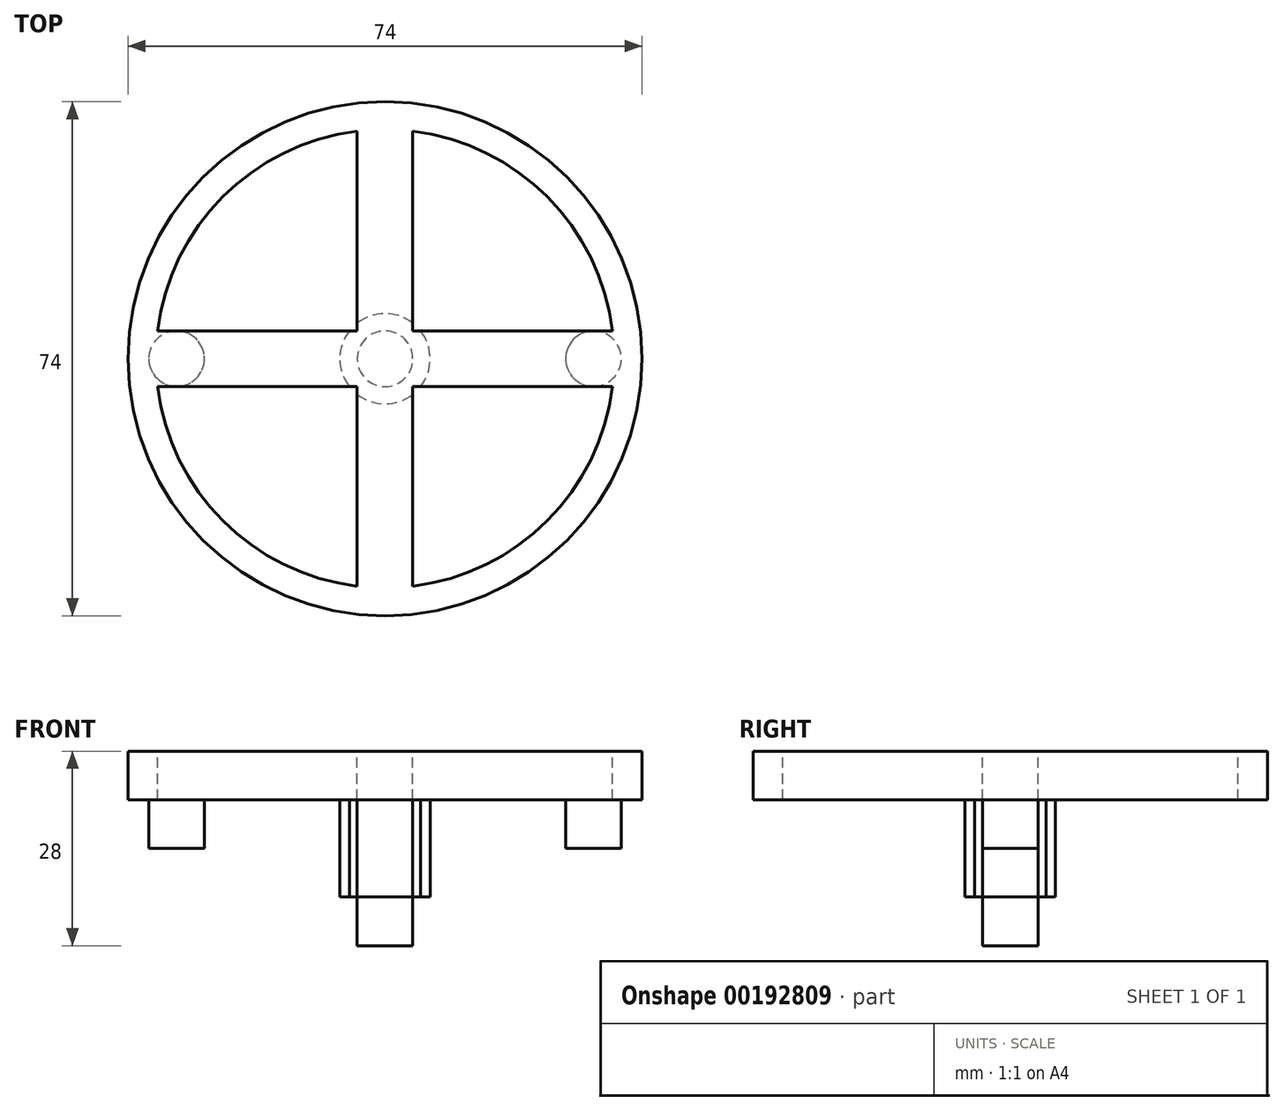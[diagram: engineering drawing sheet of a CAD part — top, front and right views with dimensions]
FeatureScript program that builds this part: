
annotation { "Feature Type Name" : "Feature", "Feature Type Description" : "" }
export const myFeature = defineFeature(function(context is Context, id is Id, definition is map)
    precondition{}
    {
        {
            var Q0;
            Q0=qCreatedBy(makeId("Top.planeOp"),FACE);
            var sketch = newSketch(context, id + "F0", { "sketchPlane" : qUnion([Q0])});
            skCircle(sketch, "E0", {"center": v(0, 0) * mm, "radius": 37 * mm});
            skSolve(sketch);
        }
        {
            var Q0;
            Q0 = qSketchRegion(id + "F0", true);
            extrude(context, id + "F1", {"entities" : qUnion([Q0]), "depth" : 7 * mm});
        }
        {
            var Q0;
            Q0=makeQuery(id+"F1.opExtrude","CAP_FACE",FACE,{"disambiguationData":[OSD([sQuery(id+"F0.wireOp",EDGE,"E0")])],"isStart":true});
            var sketch = newSketch(context, id + "F2", { "sketchPlane" : qUnion([Q0])});
            skCircle(sketch, "E1", {"center": v(0, 0) * mm, "radius": 4 * mm});
            skSolve(sketch);
        }
        {
            var Q0;
            Q0 = qSketchRegion(id + "F2", true);
            extrude(context, id + "F3", {"entities" : qUnion([Q0]), "operationType" : NewBodyOperationType.ADD, "depth" : 21 * mm});
        }
        {
            var Q0;
            Q0=makeQuery(id+"F1.opExtrude","CAP_FACE",FACE,{"disambiguationData":[OSD([sQuery(id+"F0.wireOp",EDGE,"E0")])],"isStart":true});
            var sketch = newSketch(context, id + "F4", { "sketchPlane" : qUnion([Q0])});
            skCircle(sketch, "E2", {"center": v(-30, 0) * mm, "radius": 4 * mm});
            skCircle(sketch, "E3", {"center": v(30, 0) * mm, "radius": 4 * mm});
            skSolve(sketch);
        }
        {
            var Q0;
            Q0 = qSketchRegion(id + "F4", true);
            extrude(context, id + "F5", {"entities" : qUnion([Q0]), "operationType" : NewBodyOperationType.ADD, "depth" : 7 * mm});
        }
        {
            var Q0;
            Q0=makeQuery(id+"F1.opExtrude","CAP_FACE",FACE,{"disambiguationData":[OSD([sQuery(id+"F0.wireOp",EDGE,"E0")])],"isStart":true});
            var sketch = newSketch(context, id + "F6", { "sketchPlane" : qUnion([Q0])});
            skCircle(sketch, "E4", {"center": v(0, 0) * mm, "radius": 6.5 * mm});
            skSolve(sketch);
        }
        {
            var Q0;
            Q0 = qSketchRegion(id + "F6", true);
            extrude(context, id + "F7", {"entities" : qUnion([Q0]), "operationType" : NewBodyOperationType.ADD, "depth" : 14 * mm});
        }
        {
            var Q0;
            Q0=makeQuery(id+"F1.opExtrude","CAP_FACE",FACE,{"disambiguationData":[OSD([sQuery(id+"F0.wireOp",EDGE,"E0")])],"isStart":false});
            var sketch = newSketch(context, id + "F8", { "sketchPlane" : qUnion([Q0])});
            skArc(sketch, "E5", {"start": v(-32.76, -4) * mm, "mid": v(-23.33, -23.33) * mm, "end": v(-4, -32.76) * mm});
            skLineSegment(sketch, "E6", {"start": v(-32.76, -4) * mm, "end": v(-4, -4) * mm});
            skLineSegment(sketch, "E7", {"start": v(-4, -4) * mm, "end": v(-4, -32.76) * mm});
            skLineSegment(sketch, "E8.MirrorCS", {"start": v(-4, 4) * mm, "end": v(-4, 32.76) * mm});
            skArc(sketch, "E9.MirrorCS", {"start": v(-32.76, 4) * mm, "mid": v(-23.33, 23.33) * mm, "end": v(-4, 32.76) * mm});
            skLineSegment(sketch, "E10.MirrorCS", {"start": v(-32.76, 4) * mm, "end": v(-4, 4) * mm});
            skLineSegment(sketch, "E11.MirrorCS", {"start": v(32.76, 4) * mm, "end": v(4, 4) * mm});
            skLineSegment(sketch, "E12.MirrorCS", {"start": v(4, 4) * mm, "end": v(4, 32.76) * mm});
            skArc(sketch, "E13.MirrorCS", {"start": v(32.76, 4) * mm, "mid": v(23.33, 23.33) * mm, "end": v(4, 32.76) * mm});
            skLineSegment(sketch, "E14.MirrorCS", {"start": v(4, -4) * mm, "end": v(4, -32.76) * mm});
            skLineSegment(sketch, "E15.MirrorCS", {"start": v(32.76, -4) * mm, "end": v(4, -4) * mm});
            skArc(sketch, "E16.MirrorCS", {"start": v(32.76, -4) * mm, "mid": v(23.33, -23.33) * mm, "end": v(4, -32.76) * mm});
            skSolve(sketch);
        }
        {
            var Q0;
            Q0 = qSketchRegion(id + "F8", true);
            extrude(context, id + "F9", {"entities" : qUnion([Q0]), "operationType" : NewBodyOperationType.REMOVE, "endBound" : BoundingType.THROUGH_ALL, "oppositeDirection" : true, "depth" : 25 * mm});
        }
    });
